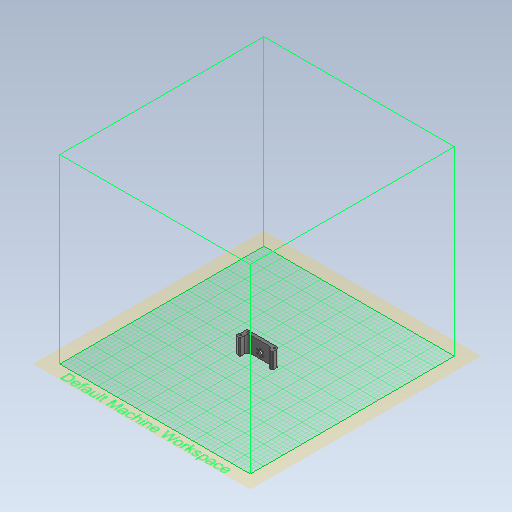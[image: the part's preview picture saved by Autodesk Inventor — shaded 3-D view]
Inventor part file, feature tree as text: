
AUTODESK INVENTOR PART (.ipt)
format: ipt  version: 2020 (Build 240168000, 168)  size: 727,040 bytes
history: native  units: mm
features: sketch x7, extrude x7, chamfer x2, projected_geometry x2, other x1, fillet x1
ambient origin geometry x8: Origin, YZ Plane, XZ Plane, XY Plane, X Axis, Y Axis, Z Axis, Center Point
bodies: Body1 (feature_tree)
feature tree (20):
  other  "Твердое тело1"
  sketch  "Эскиз1"
  extrude  "Выдавливание10"  Depth=3.8mm
  sketch  "Эскиз6"
  extrude  "Выдавливание13"  Depth=6.0mm
  extrude  "Выдавливание14"  Depth=35.0mm TaperAngle=0.0deg
  chamfer  "Фаска3"  Distance=59.0mm
  extrude  "Выдавливание15"  Depth=21.3mm
  fillet  "Сопряжение1"  Radius=15.0mm
  extrude  "Выдавливание16"  Depth=10.4mm
  extrude  "Выдавливание17"  Depth=2.5mm
  sketch  "Эскиз10"
  extrude  "Выдавливание18"  Depth=60.0mm TaperAngle=360.0deg
  chamfer  "Фаска4"  Distance=33.5mm
  sketch  "Эскиз7"
  sketch  "Эскиз8"
  projected_geometry  "Спроецированная петля3"
  sketch  "Эскиз9"
  projected_geometry  "Спроецированная петля4"
  sketch  "Эскиз11"
